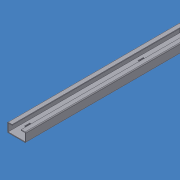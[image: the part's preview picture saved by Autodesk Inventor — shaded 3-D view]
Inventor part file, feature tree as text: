
AUTODESK INVENTOR PART (.ipt)
format: ipt  version: 2015 (Build 190159000, 159)  size: 248,832 bytes
history: native  units: mm
features: sheet_metal_op x9, other x8, sketch x6, plane x2
ambient origin geometry x8: Origin, YZ Plane, XZ Plane, XY Plane, X Axis, Y Axis, Z Axis, Center Point
bodies: Solid1 (feature_tree)
feature tree (25):
  sheet_metal_op  "Face1"
  sheet_metal_op  "Flange1"
  sheet_metal_op  "Flange2"
  sheet_metal_op  "Flange3"
  sheet_metal_op  "Flange4"
  plane  "Work Plane4"
  plane  "Work Plane6"
  sketch  "Sketch1"  dims[d4=0.001mm]
  other  "Plate1"
  sketch  "Sketch2"  dims[d5=3.0mm]
  other  "Plate2"
  sheet_metal_op  "Bend1"
  sketch  "Sketch3"  dims[d6=0.001mm]
  other  "Plate3"
  sheet_metal_op  "Bend2"
  sketch  "Sketch4"  dims[d7=6.0mm]
  other  "Plate4"
  sheet_metal_op  "Bend3"
  sketch  "Sketch5"  dims[d8=0.001mm]
  other  "Plate5"
  sheet_metal_op  "Bend4"
  sketch  "Sketch6"  dims[d9=29.0mm d10=90.0deg d11=0.001mm d12=3.0mm d13=0.001mm d14=6.0mm d15=0.001mm d16=29.0mm d17=90.0deg d18=0.001mm d19=3.0mm d20=0.001mm d21=6.0mm d22=0.001mm d23=15.0mm d24=90.0deg d25=0.001mm d26=3.0mm d27=0.001mm d28=6.0mm d29=0.001mm d30=15.0mm d31=90.0deg d32=0.001mm d33=4.0mm d34=20.5mm d35=4.0mm d36=20.5mm d37=0.0mm d38=33.0mm d40=4.0mm d41=0.0mm d42=650.0mm d45=150.0mm d46=10.0mm d47=10.0mm d48=64.0mm d49=6.0mm d50=64.0mm d51=4.0mm d52=9.0mm d62=20.5mm d63=4.0mm d64=9.0mm d65=20.5mm d66=4.0mm d68=4.0mm d69=0.0mm d71=50.0mm d72=33.0mm d73=16.5mm d0=3.0mm]
  other  "FlatPattern"
  other  "Cut1"
  other  "FlatPatternExtrusion2"
